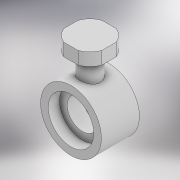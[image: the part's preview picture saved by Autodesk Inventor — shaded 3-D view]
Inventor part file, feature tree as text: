
AUTODESK INVENTOR PART (.ipt)
format: ipt  version: 2022 (Build 260153000, 153)  size: 200,704 bytes
history: native  units: mm
features: sketch x9, extrude x7, projected_geometry x3, revolve x1
ambient origin geometry x8: Origin, YZ Plane, XZ Plane, XY Plane, X Axis, Y Axis, Z Axis, Center Point
bodies: Solid1 (feature_tree)
feature tree (20):
  sketch  "Sketch1"  dims[d0=7.5mm d1=4.0mm d2=8.0mm]
  revolve  "Revolution1"  [1 undecoded]
  extrude  "Extrusion1"  Depth=2.5mm
  extrude  "Extrusion2"  Depth=0.75mm
  extrude  "Extrusion3"  Depth=7.5mm
  extrude  "Extrusion4"  Depth=12.0mm TaperAngle=0.0deg
  extrude  "Extrusion5"  Depth=3.0mm TaperAngle=0.0deg
  extrude  "Extrusion6"  Depth=8.25mm TaperAngle=0.0deg
  extrude  "Extrusion7"  Depth=7.5mm
  sketch  "Sketch2"  dims[d3=2.5mm d4=4.1mm]
  sketch  "Sketch3"  dims[d5=90.0deg d6=0.75mm]
  sketch  "Sketch4"  dims[d7=12.0mm d8=7.5mm]
  projected_geometry  "Projected Loop1"
  sketch  "Sketch6"  dims[d9=12.0mm d10=0.0mm d11=12.0mm d12=0.0mm]
  sketch  "Sketch7"  dims[d13=6.0mm d14=3.0mm d15=0.0mm]
  sketch  "Sketch8"  dims[d16=9.0mm d17=8.25mm d18=0.0mm]
  sketch  "Sketch9"  dims[d19=8.25mm d20=0.0mm d23=7.5mm]
  projected_geometry  "Projected Loop2"
  sketch  "Sketch10"  dims[d24=10.0mm d25=0.0mm d26=10.0mm d27=0.0mm]
  projected_geometry  "Projected Loop3"
note: 1 required parameter value undecoded (feature->parameter linkage not recoverable at this tier; creation-order binding heuristic only, values carry confidence <= 0.55)
